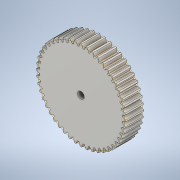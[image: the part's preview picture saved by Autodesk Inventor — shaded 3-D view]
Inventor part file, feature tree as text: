
AUTODESK INVENTOR PART (.ipt)
format: ipt  version: 2021 (Build 250183000, 183)  size: 359,936 bytes
history: native  units: mm (DEFAULTED — no unit token found)
features: plane x3, other x3, sketch x3, extrude x1, hole x1
ambient origin geometry x8: Origin, YZ Plane, XZ Plane, XY Plane, X Axis, Y Axis, Z Axis, Center Point
bodies: Solid1 (feature_tree)
feature tree (11):
  extrude  "Extrusion1"  Depth=8.0mm TaperAngle=0.0deg
  plane  "Work Plane2"
  plane  "Work Plane8"
  plane  "Work Plane9"
  other  "Spur Gear"
  hole  "Hole1"  [1 undecoded]
  sketch  "Sketch1"  dims[d0=39.68mm d1=8.0mm d2=0.0mm]
  sketch  "Sketch2"  dims[d3=38.4mm d4=10.0mm d5=0.0mm]
  other  "Srf1"
  sketch  "Sketch3"  dims[d16=28.8mm d17=0.0mm d34=0.654498mm d39=0.0mm d41=0.0mm d43=28.8mm d46=28.8mm d47=0.0mm d48=0.0mm d49=3.0mm d50=3.0mm d51=6.0mm d52=4.0mm d53=2.0mm d54=90.0deg d55=8.0mm d56=20.594885mm]
  other  "Pitch Diameter"
note: 1 required parameter value undecoded (feature->parameter linkage not recoverable at this tier; creation-order binding heuristic only, values carry confidence <= 0.55)
